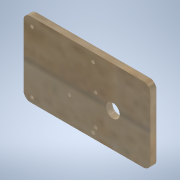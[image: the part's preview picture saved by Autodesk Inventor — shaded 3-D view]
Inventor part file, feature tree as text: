
AUTODESK INVENTOR PART (.ipt)
format: ipt  version: 2020.3 (Build 243373000, 373)  size: 172,544 bytes
history: native  units: mm
features: sketch x5, hole x3, extrude x2, other x1, fillet x1
ambient origin geometry x8: Origin, YZ Plane, XZ Plane, XY Plane, X Axis, Y Axis, Z Axis, Center Point
bodies: Body1 (feature_tree)
feature tree (12):
  other  "ソリッド1"
  extrude  "押し出し1"  Depth=112.0mm
  hole  "穴1"  [1 undecoded]
  fillet  "フィレット1"  Radius=5.5mm
  hole  "穴2"  [1 undecoded]
  hole  "穴3"  [1 undecoded]
  extrude  "押し出し2"  Depth=7.5mm
  sketch  "スケッチ1"
  sketch  "スケッチ2"
  sketch  "スケッチ3"
  sketch  "スケッチ4"
  sketch  "スケッチ5"
note: 3 required parameter values undecoded (feature->parameter linkage not recoverable at this tier; creation-order binding heuristic only, values carry confidence <= 0.55)
